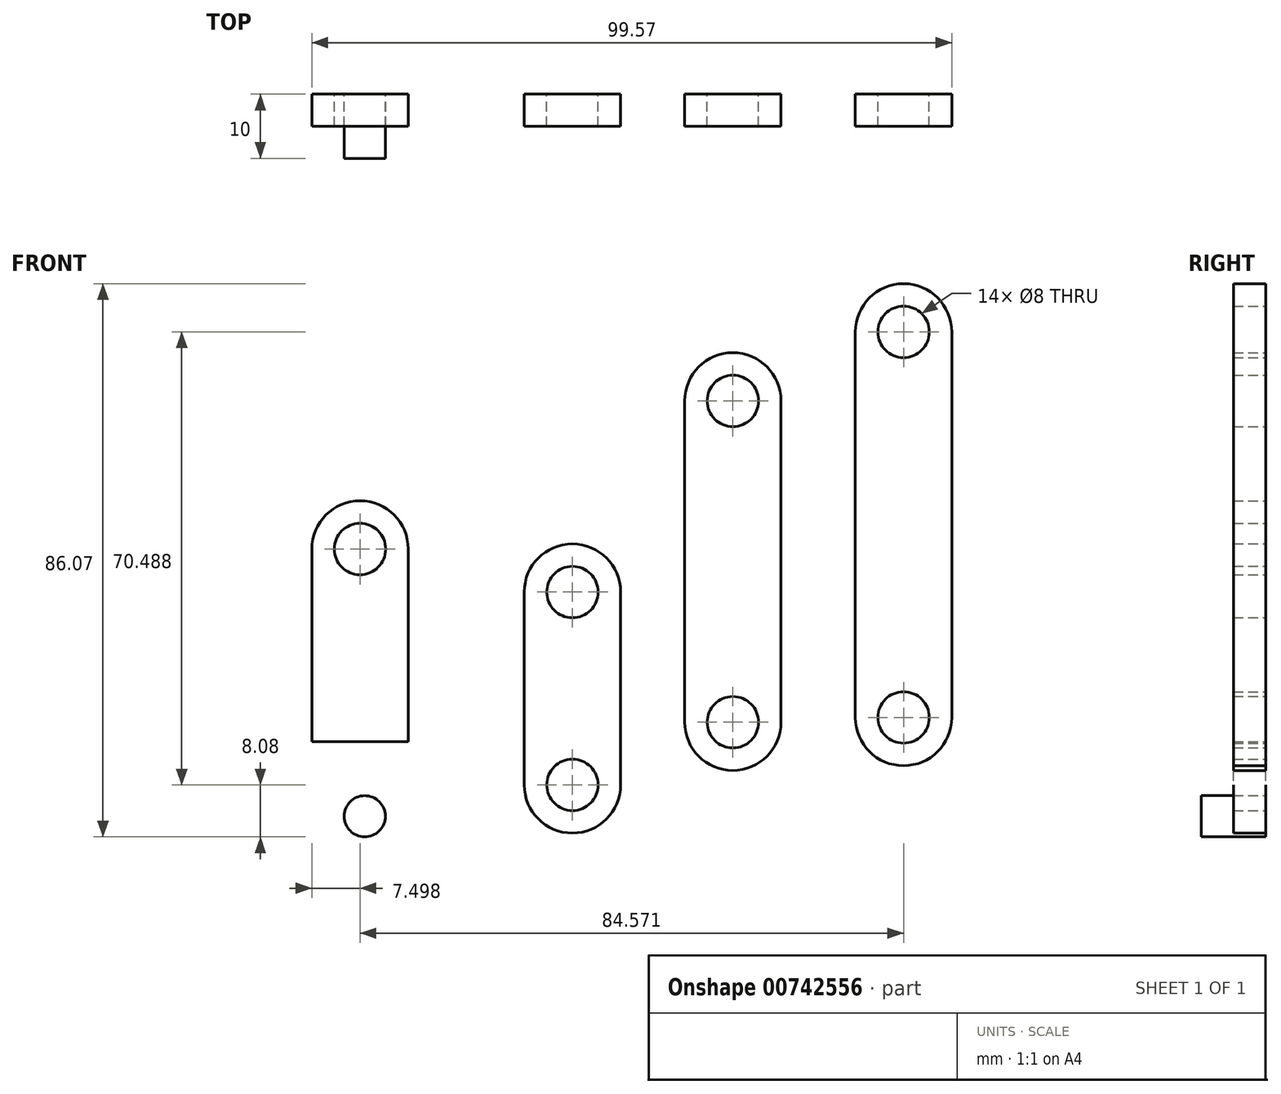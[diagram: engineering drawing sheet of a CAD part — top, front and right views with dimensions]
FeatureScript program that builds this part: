
annotation { "Feature Type Name" : "Feature", "Feature Type Description" : "" }
export const myFeature = defineFeature(function(context is Context, id is Id, definition is map)
    precondition{}
    {
        {
            var Q0;
            Q0=qCreatedBy(makeId("Front.planeOp"),FACE);
            var sketch = newSketch(context, id + "F0", { "sketchPlane" : qUnion([Q0])});
            skLineSegment(sketch, "E0.left", {"start": v(-66.56, 36.7) * mm, "end": v(-66.56, 6.7) * mm});
            skLineSegment(sketch, "E0.right", {"start": v(-51.56, 36.7) * mm, "end": v(-51.56, 6.7) * mm});
            skArc(sketch, "E1", {"start": v(-51.56, 36.7) * mm, "mid": v(-59.06, 44.2) * mm, "end": v(-66.56, 36.7) * mm});
            skCircle(sketch, "E2", {"center": v(-59.06, 36.7) * mm, "radius": 4 * mm});
            skLineSegment(sketch, "E3.left", {"start": v(-33.51, 30) * mm, "end": v(-33.51, 0) * mm});
            skLineSegment(sketch, "E3.right", {"start": v(-18.51, 30) * mm, "end": v(-18.51, 0) * mm});
            skArc(sketch, "E4", {"start": v(-18.51, 30) * mm, "mid": v(-26.01, 37.5) * mm, "end": v(-33.51, 30) * mm});
            skArc(sketch, "E5", {"start": v(-33.51, 0) * mm, "mid": v(-26.01, -7.5) * mm, "end": v(-18.51, 0) * mm});
            skCircle(sketch, "E6", {"center": v(-26.01, 0) * mm, "radius": 4 * mm});
            skLineSegment(sketch, "E7.left", {"start": v(-8.55, 59.75) * mm, "end": v(-8.55, 9.75) * mm});
            skLineSegment(sketch, "E7.right", {"start": v(6.45, 59.75) * mm, "end": v(6.45, 9.75) * mm});
            skArc(sketch, "E8", {"start": v(6.45, 59.75) * mm, "mid": v(-1.05, 67.25) * mm, "end": v(-8.55, 59.75) * mm});
            skArc(sketch, "E9", {"start": v(-8.55, 9.75) * mm, "mid": v(-1.05, 2.25) * mm, "end": v(6.45, 9.75) * mm});
            skCircle(sketch, "E10", {"center": v(-1.05, 9.75) * mm, "radius": 4 * mm});
            skCircle(sketch, "E11", {"center": v(-1.05, 59.75) * mm, "radius": 4 * mm});
            skLineSegment(sketch, "E12.left", {"start": v(18, 70.49) * mm, "end": v(18, 10.49) * mm});
            skLineSegment(sketch, "E12.right", {"start": v(33, 70.49) * mm, "end": v(33, 10.49) * mm});
            skArc(sketch, "E13", {"start": v(33, 70.49) * mm, "mid": v(25.5, 77.99) * mm, "end": v(18, 70.49) * mm});
            skCircle(sketch, "E14", {"center": v(25.5, 70.49) * mm, "radius": 4 * mm});
            skArc(sketch, "E15", {"start": v(18, 10.49) * mm, "mid": v(25.5, 2.99) * mm, "end": v(33, 10.49) * mm});
            skCircle(sketch, "E16", {"center": v(25.5, 10.49) * mm, "radius": 4 * mm});
            skCircle(sketch, "E17", {"center": v(-26.01, 30) * mm, "radius": 4 * mm});
            skLineSegment(sketch, "E18.trimOffspring", {"start": v(-22.01, 0) * mm, "end": v(-18.51, 0) * mm});
            skLineSegment(sketch, "E19", {"start": v(-66.56, 6.7) * mm, "end": v(-51.56, 6.7) * mm});
            skPoint(sketch, "E20.center.orphan", {"position": v(-59.06, 6.7) * mm});
            skCircle(sketch, "E21", {"center": v(-58.32, -4.88) * mm, "radius": 3.2 * mm});
            skSolve(sketch);
        }
        {
            var Q0;
            Q0=makeQuery(id+"F0.imprint","IMPRINT",FACE,{"disambiguationData":[TD([[makeQuery(id+"F0.imprint","IMPRINT",EDGE,{"derivedFrom":sQuery(id+"F0.wireOp",EDGE,"E0.left")}),1.0]])]});
            var Q1;
            Q1=makeQuery(id+"F0.imprint","IMPRINT",FACE,{"disambiguationData":[TD([[makeQuery(id+"F0.imprint","IMPRINT",EDGE,{"derivedFrom":sQuery(id+"F0.wireOp",EDGE,"E3.left")}),1.0]])]});
            var Q2;
            Q2=makeQuery(id+"F0.imprint","IMPRINT",FACE,{"disambiguationData":[TD([[makeQuery(id+"F0.imprint","IMPRINT",EDGE,{"derivedFrom":sQuery(id+"F0.wireOp",EDGE,"E7.left")}),1.0]])]});
            var Q3;
            Q3=makeQuery(id+"F0.imprint","IMPRINT",FACE,{"disambiguationData":[TD([[makeQuery(id+"F0.imprint","IMPRINT",EDGE,{"derivedFrom":sQuery(id+"F0.wireOp",EDGE,"E12.left")}),1.0]])]});
            extrude(context, id + "F1", {"entities" : qUnion([Q0, Q1, Q2, Q3]), "depth" : 5 * mm, "offsetDistance" : 25 * mm});
        }
        {
            var Q0;
            Q0 = qSketchRegion(id + "F0", true);
            extrude(context, id + "F2", {"entities" : qUnion([Q0]), "depth" : 5 * mm, "offsetDistance" : 25 * mm});
        }
        {
            var Q0;
            Q0=makeQuery(id+"F2.opExtrude","CAP_FACE",FACE,{"disambiguationData":[OSD([sQuery(id+"F0.wireOp",EDGE,"E21")])],"isStart":false});
            var Q1;
            Q1=makeQuery(id+"F2.opExtrude","CAP_FACE",FACE,{"disambiguationData":[OSD([sQuery(id+"F0.wireOp",EDGE,"E21")])],"isStart":true});
            extrude(context, id + "F3", {"entities" : qUnion([Q0, Q1]), "operationType" : NewBodyOperationType.ADD, "depth" : 5 * mm, "offsetDistance" : 25 * mm});
        }
    });
